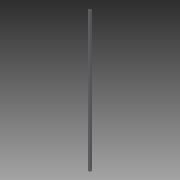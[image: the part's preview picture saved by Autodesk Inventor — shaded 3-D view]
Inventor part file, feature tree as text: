
AUTODESK INVENTOR PART (.ipt)
format: ipt  version: 2015 SP1 (Build 190203100, 203)  size: 81,920 bytes
history: native  units: mm
features: other x3, sketch x3
ambient origin geometry x8: Origin, YZ Plane, XZ Plane, XY Plane, X Axis, Y Axis, Z Axis, Center Point
bodies: Solid1 (feature_tree)
feature tree (6):
  other  "Pied.ipt"
  other  "Solid1::Pied.ipt"
  other  "TaggingFeature1"
  sketch  "Sketch1"  dims[d0=10.0mm]
  sketch  "Sketch2"
  sketch  "Sketch3"
